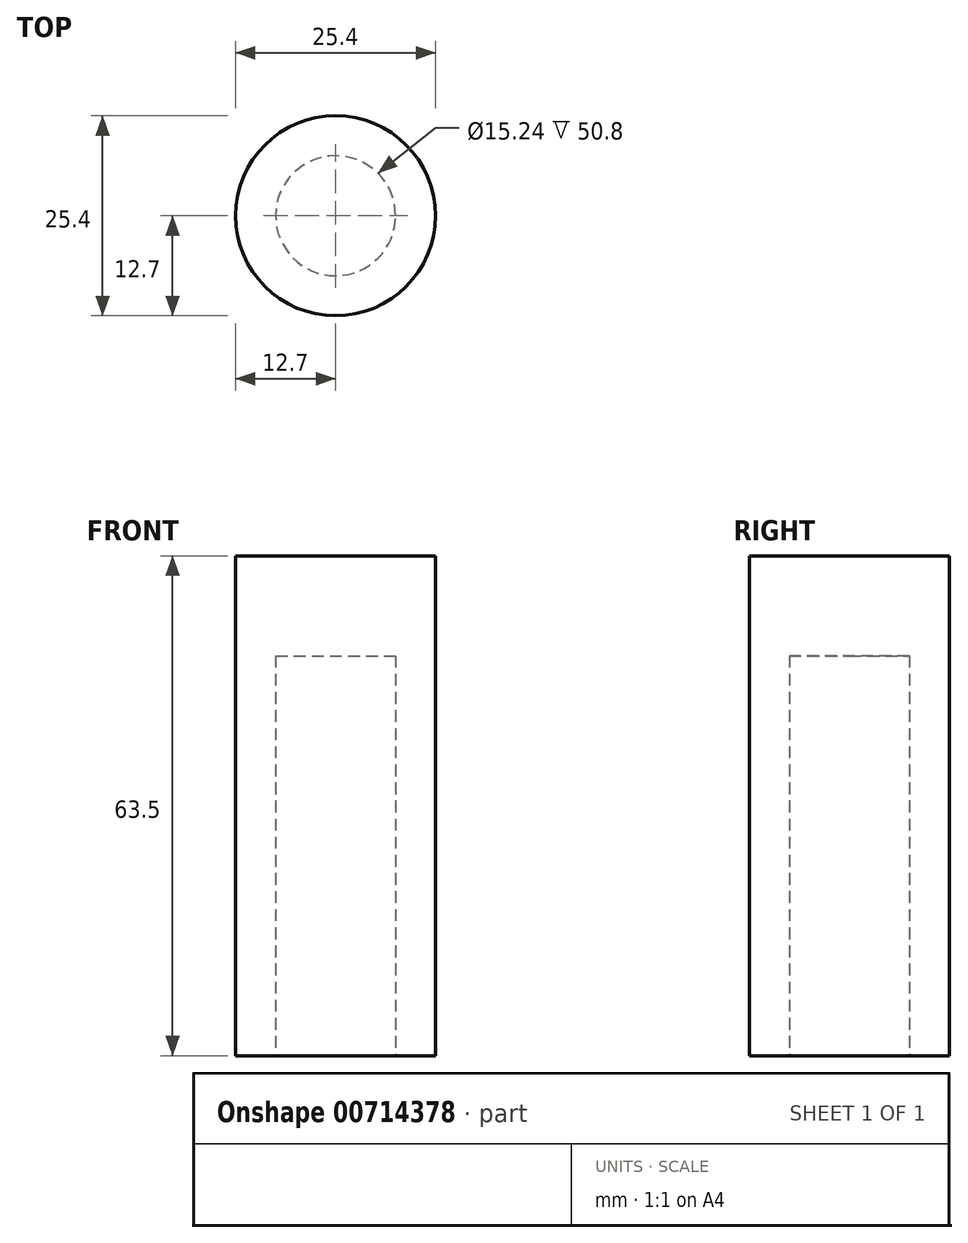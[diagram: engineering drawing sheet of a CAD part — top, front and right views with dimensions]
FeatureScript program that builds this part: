
annotation { "Feature Type Name" : "Feature", "Feature Type Description" : "" }
export const myFeature = defineFeature(function(context is Context, id is Id, definition is map)
    precondition{}
    {
        {
            var Q0;
            Q0=qCreatedBy(makeId("Front.planeOp"),FACE);
            var sketch = newSketch(context, id + "F0", { "sketchPlane" : qUnion([Q0])});
            skLineSegment(sketch, "E0", {"start": v(0, 0) * mm, "end": v(0, 63.5) * mm, "construction": true});
            skLineSegment(sketch, "E1", {"start": v(7.62, 0) * mm, "end": v(12.7, 0) * mm});
            skLineSegment(sketch, "E2", {"start": v(12.7, 0) * mm, "end": v(12.7, 63.5) * mm});
            skLineSegment(sketch, "E3", {"start": v(12.7, 63.5) * mm, "end": v(0, 63.5) * mm});
            skLineSegment(sketch, "E4", {"start": v(0, 63.5) * mm, "end": v(0, 50.8) * mm});
            skLineSegment(sketch, "E5", {"start": v(0, 50.8) * mm, "end": v(7.62, 50.8) * mm});
            skLineSegment(sketch, "E6", {"start": v(7.62, 50.8) * mm, "end": v(7.62, 0) * mm});
            skSolve(sketch);
        }
        {
            var Q0;
            Q0=makeQuery(id+"F0.imprint","IMPRINT",FACE,{"disambiguationData":[TD([[makeQuery(id+"F0.imprint","IMPRINT",EDGE,{"derivedFrom":sQuery(id+"F0.wireOp",EDGE,"E1")}),1.0]])]});
            var Q1;
            Q1=sQuery(id+"F0.wireOp",EDGE,"E0");
            revolve(context, id + "F1", {"surfaceOperationType" : NewSurfaceOperationType.NEW, "entities" : qUnion([Q0]), "axis" : qUnion([Q1]), "revolveType" : RevolveType.FULL});
        }
    });
